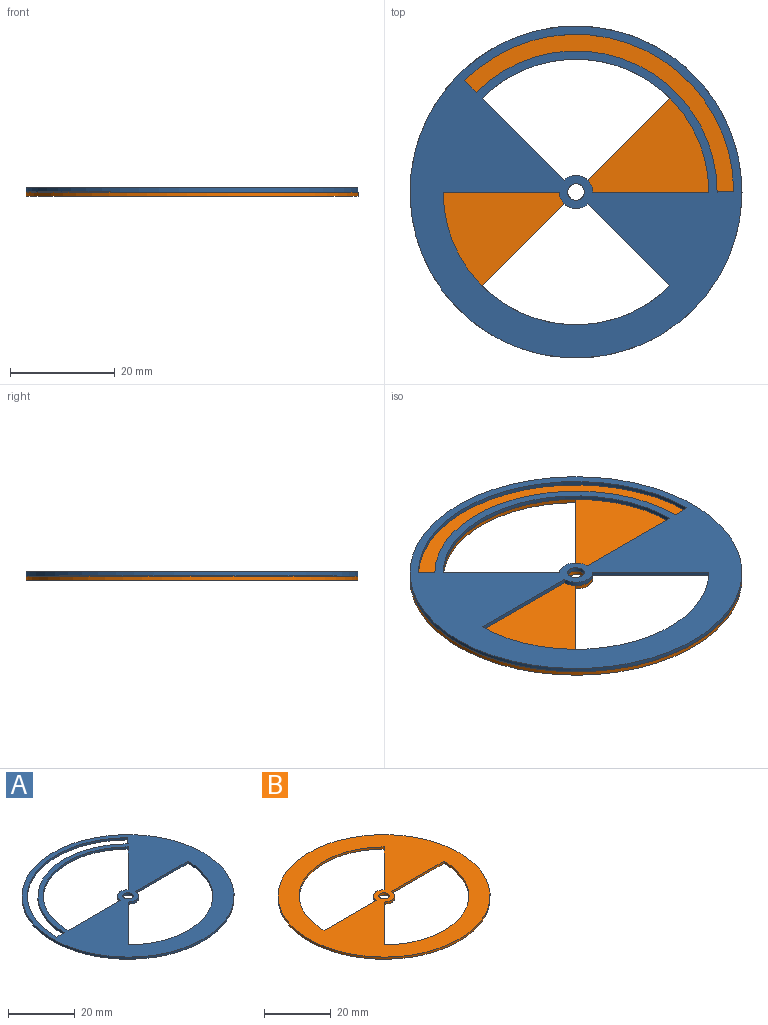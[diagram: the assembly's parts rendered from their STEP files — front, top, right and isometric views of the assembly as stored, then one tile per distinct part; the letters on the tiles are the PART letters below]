
ASSEMBLY  parts=2 mates=1
PART A: 16 faces, bbox 63.5x63.5x0.8 mm
  f0: plane 15.72x15.72mm, normal (0.71,-0.71,0), area 17.6mm2, adj f1,f13,f14,f15
  f1: cylinder r=3.17mm len=5.42mm, axis (0,0,-1), area 5.9mm2, adj f0,f2,f14,f15
  f2: plane 22.23x0.79mm, normal (0,-1,0), area 17.6mm2, adj f1,f13,f14,f15
  f3: cylinder r=26.99mm len=46.07mm, axis (0,0,-1), area 50.5mm2, adj f4,f9,f14,f15
  f4: plane 3.18x0.79mm, normal (0,1,0), area 2.5mm2, adj f3,f5,f14,f15
  f5: cylinder r=30.16mm len=51.39mm, axis (0,0,-1), area 56.3mm2, adj f4,f9,f14,f15
  f6: cylinder r=25.4mm len=43.36mm, axis (0,0,-1), area 47.5mm2, adj f7,f12,f14,f15
  f7: plane 15.72x15.72mm, normal (-0.71,0.71,0), area 17.6mm2, adj f6,f8,f14,f15
  f8: cylinder r=3.17mm len=5.42mm, axis (0,0,-1), area 5.9mm2, adj f7,f12,f14,f15
  f9: plane 2.34x2.15mm, normal (-0.74,0.68,0), area 2.5mm2, adj f3,f5,f14,f15
  f10: cylinder r=31.75mm len=63.5mm, axis (0,0,-1), area 158.3mm2, adj f14,f15
  f11: cylinder r=1.59mm len=3.18mm, axis (0,0,-1), area 7.9mm2, adj f14,f15
  f12: plane 22.23x0.79mm, normal (0,1,0), area 17.6mm2, adj f6,f8,f14,f15
  f13: cylinder r=25.4mm len=43.36mm, axis (0,0,-1), area 47.5mm2, adj f0,f2,f14,f15
  f14: plane 63.5x63.5mm, normal (0,0,1), area 1449.1mm2, adj f0,f1,f2,f3,f4,f5,f6,f7
  f15: plane 63.5x63.5mm, normal (0,0,-1), area 1449.1mm2, adj f0,f1,f2,f3,f4,f5,f6,f7
PART B: 12 faces, bbox 63.5x63.5x0.8 mm
  f0: plane 15.72x15.72mm, normal (0.71,-0.71,0), area 17.6mm2, adj f1,f9,f10,f11
  f1: cylinder r=3.17mm len=5.42mm, axis (0,0,-1), area 5.9mm2, adj f0,f2,f10,f11
  f2: plane 22.23x0.79mm, normal (0,-1,0), area 17.6mm2, adj f1,f9,f10,f11
  f3: cylinder r=25.4mm len=43.36mm, axis (0,0,-1), area 47.5mm2, adj f4,f8,f10,f11
  f4: plane 15.72x15.72mm, normal (-0.71,0.71,0), area 17.6mm2, adj f3,f5,f10,f11
  f5: cylinder r=3.17mm len=5.42mm, axis (0,0,-1), area 5.9mm2, adj f4,f8,f10,f11
  f6: cylinder r=31.75mm len=63.5mm, axis (0,0,-1), area 158.3mm2, adj f10,f11
  f7: cylinder r=1.59mm len=3.18mm, axis (0,0,-1), area 7.9mm2, adj f10,f11
  f8: plane 22.23x0.79mm, normal (0,1,0), area 17.6mm2, adj f3,f5,f10,f11
  f9: cylinder r=25.4mm len=43.36mm, axis (0,0,-1), area 47.5mm2, adj f0,f2,f10,f11
  f10: plane 63.5x63.5mm, normal (0,0,1), area 1662.6mm2, adj f0,f1,f2,f3,f4,f5,f6,f7
  f11: plane 63.5x63.5mm, normal (0,0,-1), area 1662.6mm2, adj f0,f1,f2,f3,f4,f5,f6,f7
PLACE A rot(axis=(0,0,-1),45deg) t=(78.27,67.04,1.72)mm
PLACE B t=(78.27,67.04,0.93)mm fixed
MATE revolute A.f1 <-> B.f9  axis (0,0,-1) through (78.27,67.04,1.72)mm
